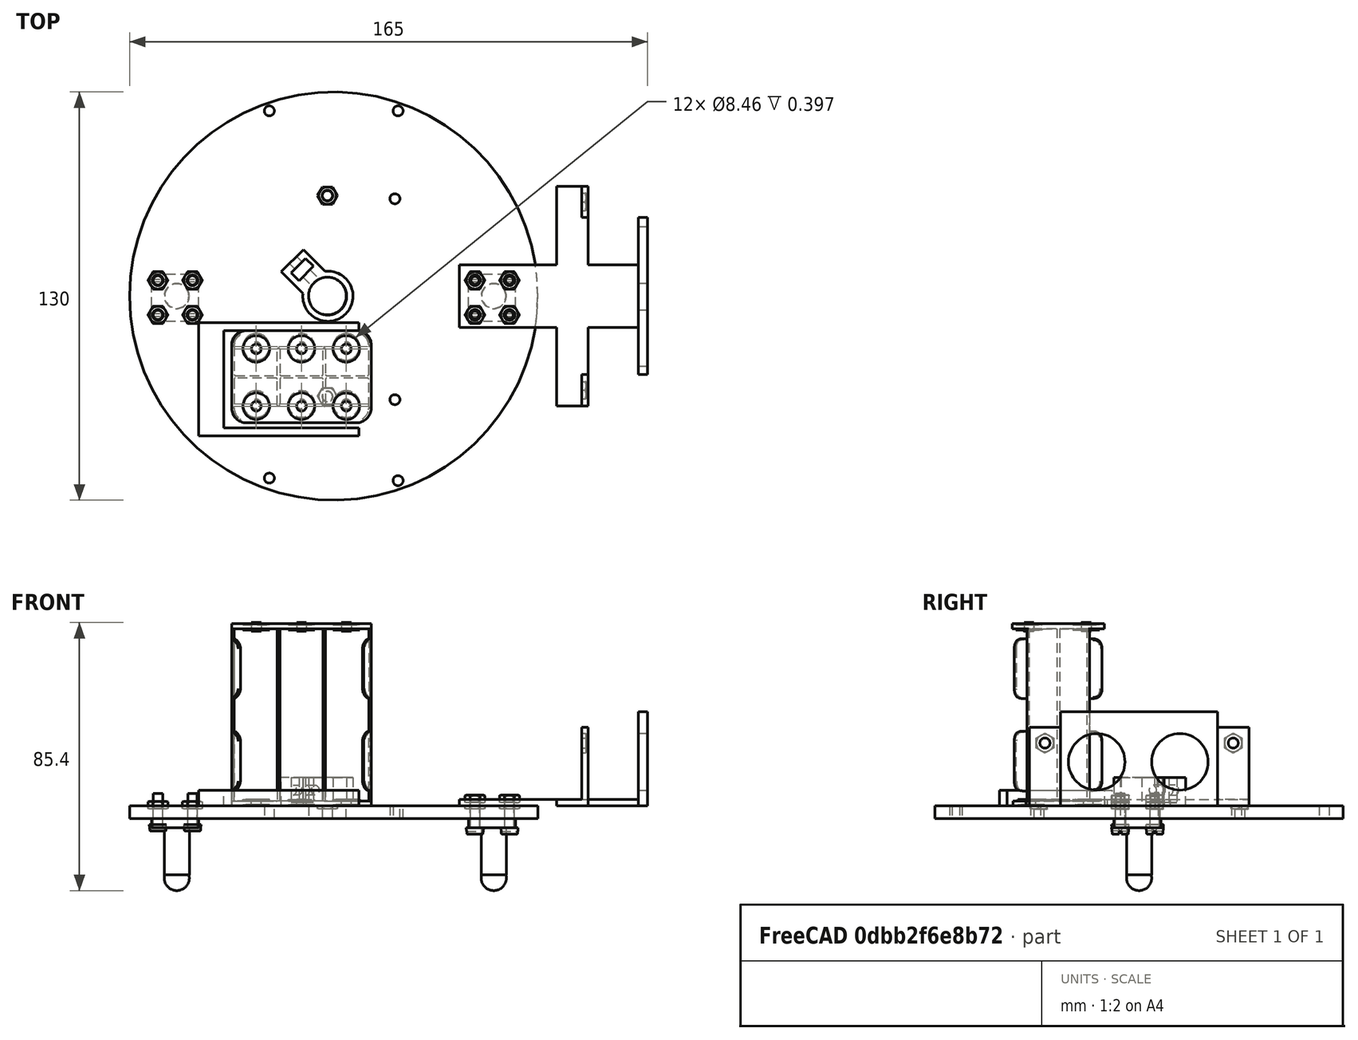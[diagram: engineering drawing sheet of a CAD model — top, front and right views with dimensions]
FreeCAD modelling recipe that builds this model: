
FCSTD DOCUMENT  (FreeCAD 0.21R33668 +26 (Git))
Label: ANIMABALLCASTER
License: All rights reserved
LicenseURL: https://en.wikipedia.org/wiki/All_rights_reserved
objects: Part::FeaturePython×16, App::DocumentObjectGroupPython×9, Part::Feature×5, Part::MultiFuse×4
note: 25 computed .brp shape members not serialized (recipe doc carries the construction recipe); baked Part::Feature solids carry a one-line shape summary decoded from their .brp

FEATURE [Part::Feature] Cut009_solid  label="ballCSensor"
  Placement = pos=(0,0,20) rot=(0,0,1;0rad)
  shape: bbox 15 x 15 x 23 mm, 13 faces (baked)
FEATURE [Part::Feature] Fusion060_solid  label="plataformaInferior (Solid)"
  Placement = pos=(0,0,20) rot=(0,0,1;0rad)
  shape: bbox 130 x 130 x 13 mm, 195 faces (baked)
FEATURE [Part::FeaturePython] Nut  label="M3-Tuerca"  # Fasteners workbench fastener (typed FeaturePython)
  Placement = pos=(41,5,8) rot=(0,0,1;0rad)
  diameter = 4
  invert = false
  leftHanded = false
  matchOuter = false
  offset = 0
  thread = false
  type = 22
FEATURE [Part::FeaturePython] Nut001  label="M3-Tuerca004"  # Fasteners workbench fastener (typed FeaturePython)
  Placement = pos=(52,5,8) rot=(0,0,1;0rad)
  diameter = 4
  invert = false
  leftHanded = false
  matchOuter = false
  offset = 0
  thread = false
  type = 22
FEATURE [Part::FeaturePython] Nut002  label="M3-Tuerca006"  # Fasteners workbench fastener (typed FeaturePython)
  Placement = pos=(52,-6,8) rot=(0,0,1;0rad)
  diameter = 4
  invert = false
  leftHanded = false
  matchOuter = false
  offset = 0
  thread = false
  type = 22
FEATURE [Part::FeaturePython] Nut003  label="M3-Tuerca005"  # Fasteners workbench fastener (typed FeaturePython)
  Placement = pos=(41,-6,8) rot=(0,0,1;0rad)
  diameter = 4
  invert = false
  leftHanded = false
  matchOuter = false
  offset = 0
  thread = false
  type = 22
FEATURE [Part::MultiFuse] Fusion  label="tuercasBallCSensor"
  Placement = pos=(0,0,2) rot=(0,0,1;0rad)
  Shapes = -> [Nut,Nut001,Nut002,Nut003]
FEATURE [Part::FeaturePython] Nut004  label="M3-Tuerca007"  # Fasteners workbench fastener (typed FeaturePython)
  Placement = pos=(41,5,8) rot=(0,0,1;0rad)
  diameter = 4
  invert = false
  leftHanded = false
  matchOuter = false
  offset = 0
  thread = false
  type = 22
FEATURE [Part::FeaturePython] Nut005  label="M3-Tuerca008"  # Fasteners workbench fastener (typed FeaturePython)
  Placement = pos=(52,5,8) rot=(0,0,1;0rad)
  diameter = 4
  invert = false
  leftHanded = false
  matchOuter = false
  offset = 0
  thread = false
  type = 22
FEATURE [Part::FeaturePython] Nut006  label="M3-Tuerca009"  # Fasteners workbench fastener (typed FeaturePython)
  Placement = pos=(52,-6,8) rot=(0,0,1;0rad)
  diameter = 4
  invert = false
  leftHanded = false
  matchOuter = false
  offset = 0
  thread = false
  type = 22
FEATURE [Part::FeaturePython] Nut007  label="M3-Tuerca010"  # Fasteners workbench fastener (typed FeaturePython)
  Placement = pos=(41,-6,8) rot=(0,0,1;0rad)
  diameter = 4
  invert = false
  leftHanded = false
  matchOuter = false
  offset = 0
  thread = false
  type = 22
FEATURE [Part::MultiFuse] Fusion001  label="tuercasBallCLibre"
  Placement = pos=(-101,0,0) rot=(0,0,1;0rad)
  Shapes = -> [Nut004,Nut005,Nut006,Nut007]
FEATURE [Part::Feature] Cut009_solid001  label="ballCLibre"
  Placement = pos=(-101,0,20) rot=(0,0,1;0rad)
  shape: bbox 15 x 15 x 23 mm, 13 faces (baked)
FEATURE [Part::Feature] Cut_solid  label="soporteSensores (Solid)"
  Placement = pos=(15,0,20) rot=(0,0,1;0rad)
  shape: bbox 60 x 70 x 30 mm, 144 faces (baked)
FEATURE [Part::FeaturePython] Screw  label="M3x10-Tornillo"  # Fasteners workbench fastener (typed FeaturePython)
  Placement = pos=(-60,5,3) rot=(1,0,0;3.14159rad)
  diameter = 4
  invert = false
  leftHanded = false
  length = 4
  lengthCustom = 10
  matchOuter = false
  offset = 0
  thread = false
  type = 30
FEATURE [Part::FeaturePython] Screw001  label="M3x10-Tornillo001"  # Fasteners workbench fastener (typed FeaturePython)
  Placement = pos=(-60,-6,3) rot=(1,0,0;3.14159rad)
  diameter = 4
  invert = false
  leftHanded = false
  length = 4
  lengthCustom = 10
  matchOuter = false
  offset = 0
  thread = false
  type = 30
FEATURE [Part::FeaturePython] Screw002  label="M3x10-Tornillo002"  # Fasteners workbench fastener (typed FeaturePython)
  Placement = pos=(-49,-6,3) rot=(1,0,0;3.14159rad)
  diameter = 4
  invert = false
  leftHanded = false
  length = 4
  lengthCustom = 10
  matchOuter = false
  offset = 0
  thread = false
  type = 30
FEATURE [Part::FeaturePython] Screw003  label="M3x10-Tornillo003"  # Fasteners workbench fastener (typed FeaturePython)
  Placement = pos=(-49,5,3) rot=(1,0,0;3.14159rad)
  diameter = 4
  invert = false
  leftHanded = false
  length = 4
  lengthCustom = 10
  matchOuter = false
  offset = 0
  thread = false
  type = 30
FEATURE [Part::MultiFuse] Fusion002  label="tornillosBallClibre"
  Shapes = -> [Screw,Screw001,Screw002,Screw003]
FEATURE [Part::FeaturePython] Screw004  label="M3x10-Tornillo004"  # Fasteners workbench fastener (typed FeaturePython)
  Placement = pos=(-60,5,3) rot=(1,0,0;3.14159rad)
  diameter = 4
  invert = false
  leftHanded = false
  length = 4
  lengthCustom = 10
  matchOuter = false
  offset = 0
  thread = false
  type = 30
FEATURE [Part::FeaturePython] Screw005  label="M3x10-Tornillo005"  # Fasteners workbench fastener (typed FeaturePython)
  Placement = pos=(-60,-6,3) rot=(1,0,0;3.14159rad)
  diameter = 4
  invert = false
  leftHanded = false
  length = 4
  lengthCustom = 10
  matchOuter = false
  offset = 0
  thread = false
  type = 30
FEATURE [Part::FeaturePython] Screw006  label="M3x10-Tornillo006"  # Fasteners workbench fastener (typed FeaturePython)
  Placement = pos=(-49,-6,3) rot=(1,0,0;3.14159rad)
  diameter = 4
  invert = false
  leftHanded = false
  length = 4
  lengthCustom = 10
  matchOuter = false
  offset = 0
  thread = false
  type = 30
FEATURE [Part::FeaturePython] Screw007  label="M3x10-Tornillo007"  # Fasteners workbench fastener (typed FeaturePython)
  Placement = pos=(-49,5,3) rot=(1,0,0;3.14159rad)
  diameter = 4
  invert = false
  leftHanded = false
  length = 4
  lengthCustom = 10
  matchOuter = false
  offset = 0
  thread = false
  type = 30
FEATURE [Part::MultiFuse] Fusion003  label="tornillosBallCSensor"
  Placement = pos=(101,0,-1) rot=(0,0,1;0rad)
  Shapes = -> [Screw004,Screw005,Screw006,Screw007]
FEATURE [App::DocumentObjectGroupPython] SimpleGroup  # scripted group (container) (typed FeaturePython)
  AnimationStepTime = 0
  AnimationSteps = 20
  Distance = 19
  Revolutions = 0
  dir_vectors = (1) [(0,0,1)]
  rot_centers = (1) [(-54.5,-0.5,-14)]
  rot_vectors = (1) [(0,0,1)]
FEATURE [App::DocumentObjectGroupPython] SimpleGroup003  # scripted group (container) (typed FeaturePython)
  AnimationStepTime = 0
  AnimationSteps = 20
  Distance = 20
  Revolutions = 0
  dir_vectors = (1) [(0,0,-1)]
  rot_centers = (1) [(-60,-6,26)]
  rot_vectors = (1) [(0,0,-1)]
FEATURE [App::DocumentObjectGroupPython] SimpleGroup004  # scripted group (container) (typed FeaturePython)
  AnimationStepTime = 0
  AnimationSteps = 20
  Distance = 40
  Revolutions = 0
  dir_vectors = (1) [(0,1.22465e-16,1)]
  rot_centers = (1) [(-60,5,-27)]
  rot_vectors = (1) [(0,1.22465e-16,1)]
FEATURE [App::DocumentObjectGroupPython] SimpleGroup005  # scripted group (container) (typed FeaturePython)
  AnimationStepTime = 0
  AnimationSteps = 20
  Distance = 19
  Revolutions = 0
  dir_vectors = (1) [(0,0,1)]
  rot_centers = (1) [(46.5,-0.5,-14)]
  rot_vectors = (1) [(0,0,1)]
FEATURE [Part::Feature] Part__Feature  label="6 x AAA Holder"
  Placement = pos=(-100,212,67) rot=(0.57735,0.57735,-0.57735;2.0944rad)
  shape: bbox 45.01 x 29.59 x 58.41 mm, 300 faces, 8 solids (baked)
FEATURE [App::DocumentObjectGroupPython] SimpleGroup006  # scripted group (container) (typed FeaturePython)
  AnimationStepTime = 0
  AnimationSteps = 20
  Distance = 100
  Revolutions = 0
  dir_vectors = (1) [(-1,-6.69631e-16,-2.22045e-16)]
  rot_centers = (1) [(13.5,-25.9132,38.8088)]
  rot_vectors = (1) [(-1,-6.69631e-16,-2.22045e-16)]
FEATURE [App::DocumentObjectGroupPython] SimpleGroup007  # scripted group (container) (typed FeaturePython)
  AnimationStepTime = 0
  AnimationSteps = 20
  Distance = 15
  Revolutions = 0
  dir_vectors = (1) [(0,0,-1)]
  rot_centers = (1) [(72,-3.55271e-16,24)]
  rot_vectors = (1) [(0,0,-1)]
FEATURE [App::DocumentObjectGroupPython] SimpleGroup008  # scripted group (container) (typed FeaturePython)
  AnimationStepTime = 0
  AnimationSteps = 20
  Distance = 18
  Revolutions = 0
  dir_vectors = (1) [(0,0,-1)]
  rot_centers = (1) [(52,-6,28)]
  rot_vectors = (1) [(0,0,-1)]
FEATURE [App::DocumentObjectGroupPython] SimpleGroup009  # scripted group (container) (typed FeaturePython)
  AnimationStepTime = 0
  AnimationSteps = 20
  Distance = 39
  Revolutions = 0
  dir_vectors = (1) [(0,0,1)]
  rot_centers = (1) [(52,-6,-27)]
  rot_vectors = (1) [(0,0,1)]
FEATURE [App::DocumentObjectGroupPython] ExplodedAssembly  # scripted group (container) (typed FeaturePython)
  AnimationStep = 0
  CurrentTrajectory = -1
  Group = -> [SimpleGroup,SimpleGroup003,SimpleGroup004,SimpleGroup005,SimpleGroup006,SimpleGroup007,SimpleGroup008,SimpleGroup009]
  InAnimation = false
  RemoveAllTrajectories = false
  ResetAnimation = false
